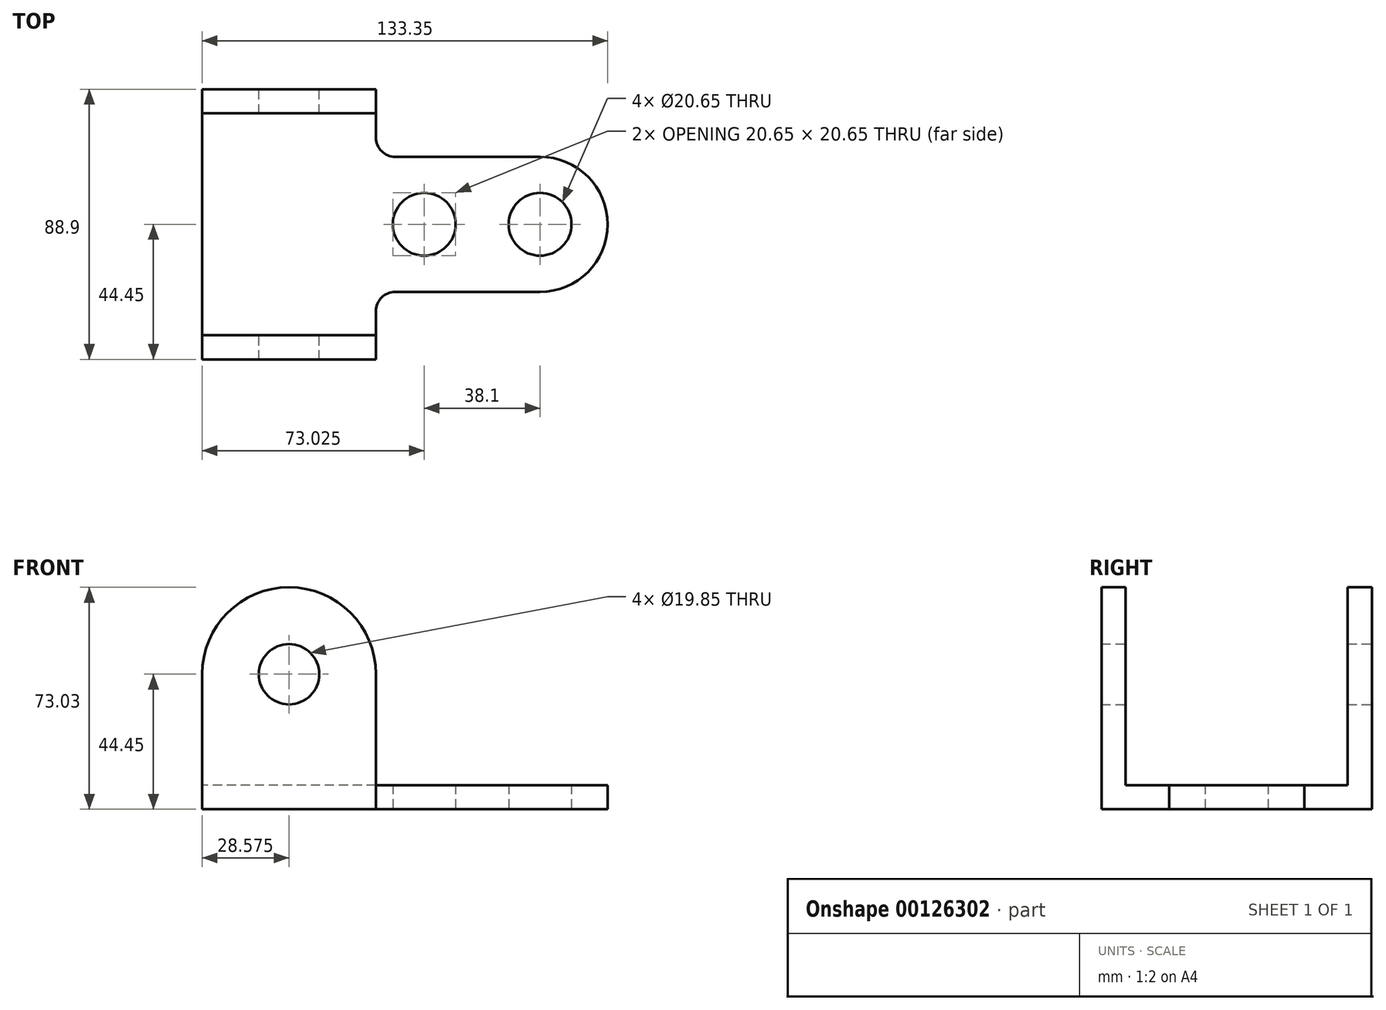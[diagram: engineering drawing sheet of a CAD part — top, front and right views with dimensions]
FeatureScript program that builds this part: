
annotation { "Feature Type Name" : "Feature", "Feature Type Description" : "" }
export const myFeature = defineFeature(function(context is Context, id is Id, definition is map)
    precondition{}
    {
        {
            var Q0;
            Q0=qCreatedBy(makeId("Front.planeOp"),FACE);
            var sketch = newSketch(context, id + "F0", { "sketchPlane" : qUnion([Q0])});
            skLineSegment(sketch, "E0", {"start": v(0, 44.45) * mm, "end": v(0, 0) * mm});
            skLineSegment(sketch, "E1", {"start": v(0, 0) * mm, "end": v(57.15, 0) * mm});
            skLineSegment(sketch, "E2", {"start": v(57.15, 0) * mm, "end": v(57.15, 44.45) * mm});
            skLineSegment(sketch, "E3", {"start": v(57.15, 0) * mm, "end": v(133.35, 0) * mm});
            skLineSegment(sketch, "E4", {"start": v(133.35, 0) * mm, "end": v(133.35, 7.94) * mm});
            skLineSegment(sketch, "E5", {"start": v(133.35, 7.94) * mm, "end": v(57.15, 7.94) * mm});
            skArc(sketch, "E6", {"start": v(0, 44.45) * mm, "mid": v(28.58, 73.03) * mm, "end": v(57.15, 44.45) * mm});
            skCircle(sketch, "E7", {"center": v(28.58, 44.45) * mm, "radius": 9.92 * mm});
            skSolve(sketch);
        }
        {
            var Q0;
            Q0 = qSketchRegion(id + "F0", true);
            extrude(context, id + "F1", {"entities" : qUnion([Q0]), "depth" : 88.9 * mm});
        }
        {
            var Q0;
            Q0=qCreatedBy(makeId("Right.planeOp"),FACE);
            var sketch = newSketch(context, id + "F2", { "sketchPlane" : qUnion([Q0])});
            skLineSegment(sketch, "E8", {"start": v(-80.96, 7.94) * mm, "end": v(-80.96, 73.03) * mm});
            skLineSegment(sketch, "E9", {"start": v(-7.94, 7.94) * mm, "end": v(-7.94, 73.03) * mm});
            skLineSegment(sketch, "E10", {"start": v(-88.9, 73.03) * mm, "end": v(0, 73.03) * mm});
            skLineSegment(sketch, "E11.0", {"start": v(0, 44.45) * mm, "end": v(0, 73.03) * mm});
            skLineSegment(sketch, "E12.0", {"start": v(-88.9, 44.45) * mm, "end": v(-88.9, 73.03) * mm});
            skLineSegment(sketch, "E13.0", {"start": v(-88.9, 7.94) * mm, "end": v(0, 7.94) * mm});
            skSolve(sketch);
        }
        {
            var Q0;
            {var subQ0=sQuery(id+"F2.wireOp",EDGE,"E8");Q0=makeQuery(id+"F2.imprint","IMPRINT",FACE,{"disambiguationData":[TD([[makeQuery(id+"F2.imprint","IMPRINT",EDGE,{"derivedFrom":subQ0}),-1.0]])]});}
            extrude(context, id + "F3", {"entities" : qUnion([Q0]), "operationType" : NewBodyOperationType.REMOVE, "depth" : 63.5 * mm});
        }
        {
            var Q0;
            Q0=qCreatedBy(makeId("Top.planeOp"),FACE);
            var sketch = newSketch(context, id + "F4", { "sketchPlane" : qUnion([Q0])});
            skCircle(sketch, "E14", {"center": v(73.03, -44.45) * mm, "radius": 10.33 * mm});
            skCircle(sketch, "E15", {"center": v(111.12, -44.45) * mm, "radius": 10.33 * mm});
            skLineSegment(sketch, "E16", {"start": v(133.35, -44.45) * mm, "end": v(0, -44.45) * mm, "construction": true});
            skLineSegment(sketch, "E17.0", {"start": v(0, -80.96) * mm, "end": v(0, -7.94) * mm});
            skLineSegment(sketch, "E18.0", {"start": v(133.35, -88.9) * mm, "end": v(133.35, 0) * mm});
            skLineSegment(sketch, "E19", {"start": v(57.15, 0) * mm, "end": v(57.15, -15.88) * mm});
            skLineSegment(sketch, "E20", {"start": v(63.5, -22.23) * mm, "end": v(111.12, -22.23) * mm});
            skLineSegment(sketch, "E21", {"start": v(57.15, -88.9) * mm, "end": v(57.15, -73.03) * mm});
            skLineSegment(sketch, "E22", {"start": v(63.5, -66.68) * mm, "end": v(111.12, -66.68) * mm});
            skArc(sketch, "E23", {"start": v(57.15, -15.88) * mm, "mid": v(59, -20.37) * mm, "end": v(63.5, -22.23) * mm});
            skArc(sketch, "E24", {"start": v(57.15, -73.03) * mm, "mid": v(59, -68.53) * mm, "end": v(63.5, -66.68) * mm});
            skArc(sketch, "E25", {"start": v(111.12, -66.68) * mm, "mid": v(133.35, -44.45) * mm, "end": v(111.12, -22.23) * mm});
            skLineSegment(sketch, "E26.0", {"start": v(133.35, 0) * mm, "end": v(57.15, 0) * mm});
            skLineSegment(sketch, "E27.0", {"start": v(133.35, -88.9) * mm, "end": v(57.15, -88.9) * mm});
            skSolve(sketch);
        }
        {
            var Q0;
            Q0 = qSketchRegion(id + "F4", true);
            extrude(context, id + "F5", {"entities" : qUnion([Q0]), "operationType" : NewBodyOperationType.REMOVE, "depth" : 25.4 * mm});
        }
    });
